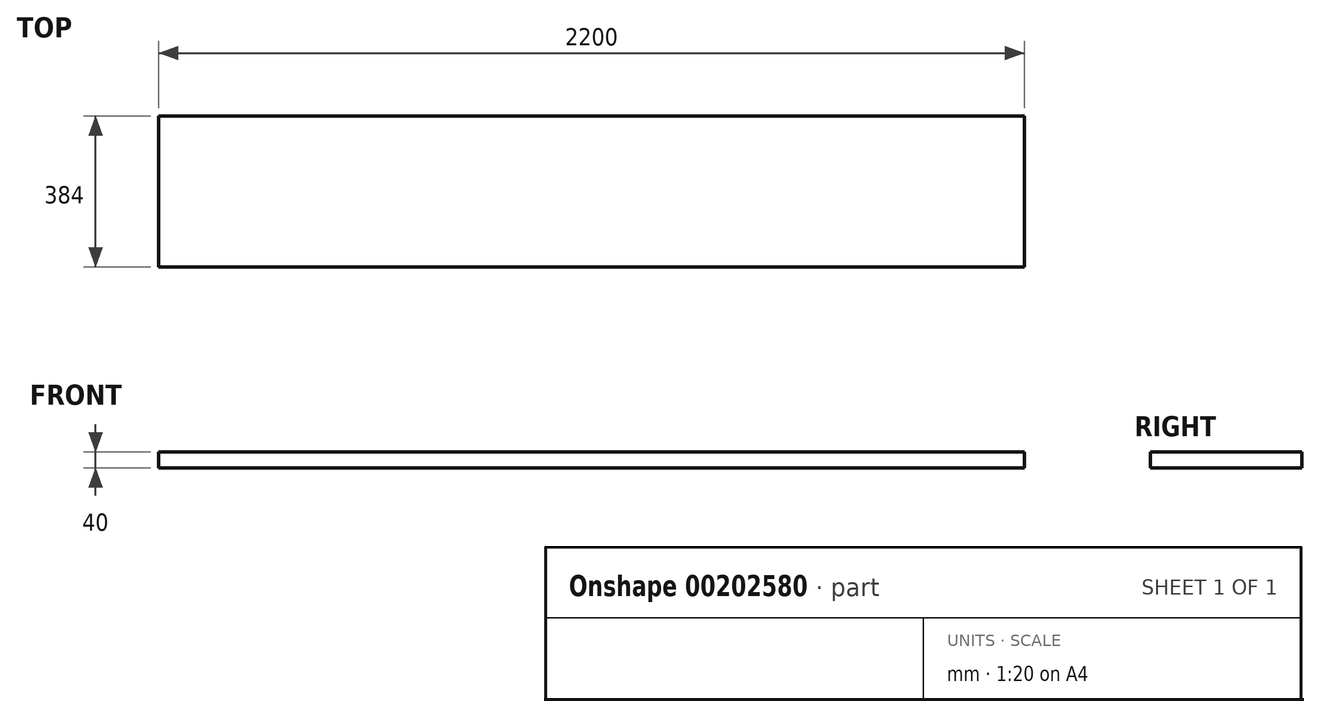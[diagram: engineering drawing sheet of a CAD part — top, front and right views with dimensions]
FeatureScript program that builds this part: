
annotation { "Feature Type Name" : "Feature", "Feature Type Description" : "" }
export const myFeature = defineFeature(function(context is Context, id is Id, definition is map)
    precondition{}
    {
        {
            var Q0;
            Q0=qCreatedBy(makeId("Top.planeOp"),FACE);
            var sketch = newSketch(context, id + "F0", { "sketchPlane" : qUnion([Q0])});
            skLineSegment(sketch, "E0.bottom", {"start": v(-864.34, -235.28) * mm, "end": v(1335.66, -235.28) * mm});
            skLineSegment(sketch, "E0.top", {"start": v(-864.34, 148.72) * mm, "end": v(1335.66, 148.72) * mm});
            skLineSegment(sketch, "E0.left", {"start": v(-864.34, -235.28) * mm, "end": v(-864.34, 148.72) * mm});
            skLineSegment(sketch, "E0.right", {"start": v(1335.66, -235.28) * mm, "end": v(1335.66, 148.72) * mm});
            skSolve(sketch);
        }
        {
            var Q0;
            Q0=makeQuery(id+"F0.imprint","IMPRINT",FACE,{"disambiguationData":[TD([[makeQuery(id+"F0.imprint","IMPRINT",EDGE,{"derivedFrom":sQuery(id+"F0.wireOp",EDGE,"E0.bottom")}),1.0]])]});
            extrude(context, id + "F1", {"entities" : qUnion([Q0]), "depth" : 40 * mm});
        }
    });
